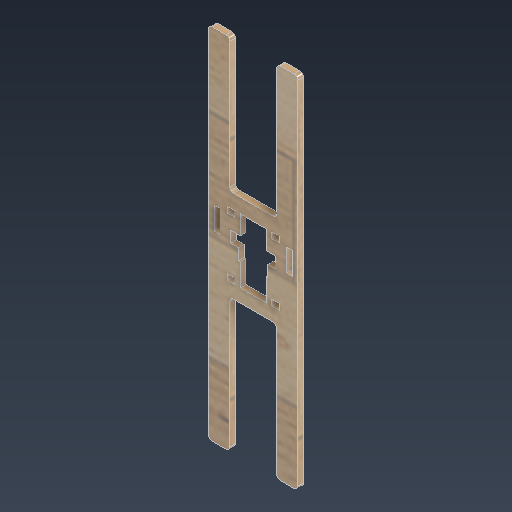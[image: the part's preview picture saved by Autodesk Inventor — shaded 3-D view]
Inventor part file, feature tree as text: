
AUTODESK INVENTOR PART (.ipt)
format: ipt  version: 2025.3 (Build 293356000, 356)  size: 259,072 bytes
history: native  units: mm
features: sketch x3, extrude x2, other x1
ambient origin geometry x8: Origin, YZ Plane, XZ Plane, XY Plane, X Axis, Y Axis, Z Axis, Center Point
bodies: Body1 (feature_tree)
feature tree (6):
  other  "實體1"
  extrude  "擠出1"  Depth=47.7mm
  sketch  "草圖3"
  extrude  "擠出4"  Depth=4.0mm
  sketch  "草圖1"
  sketch  "草圖5"
